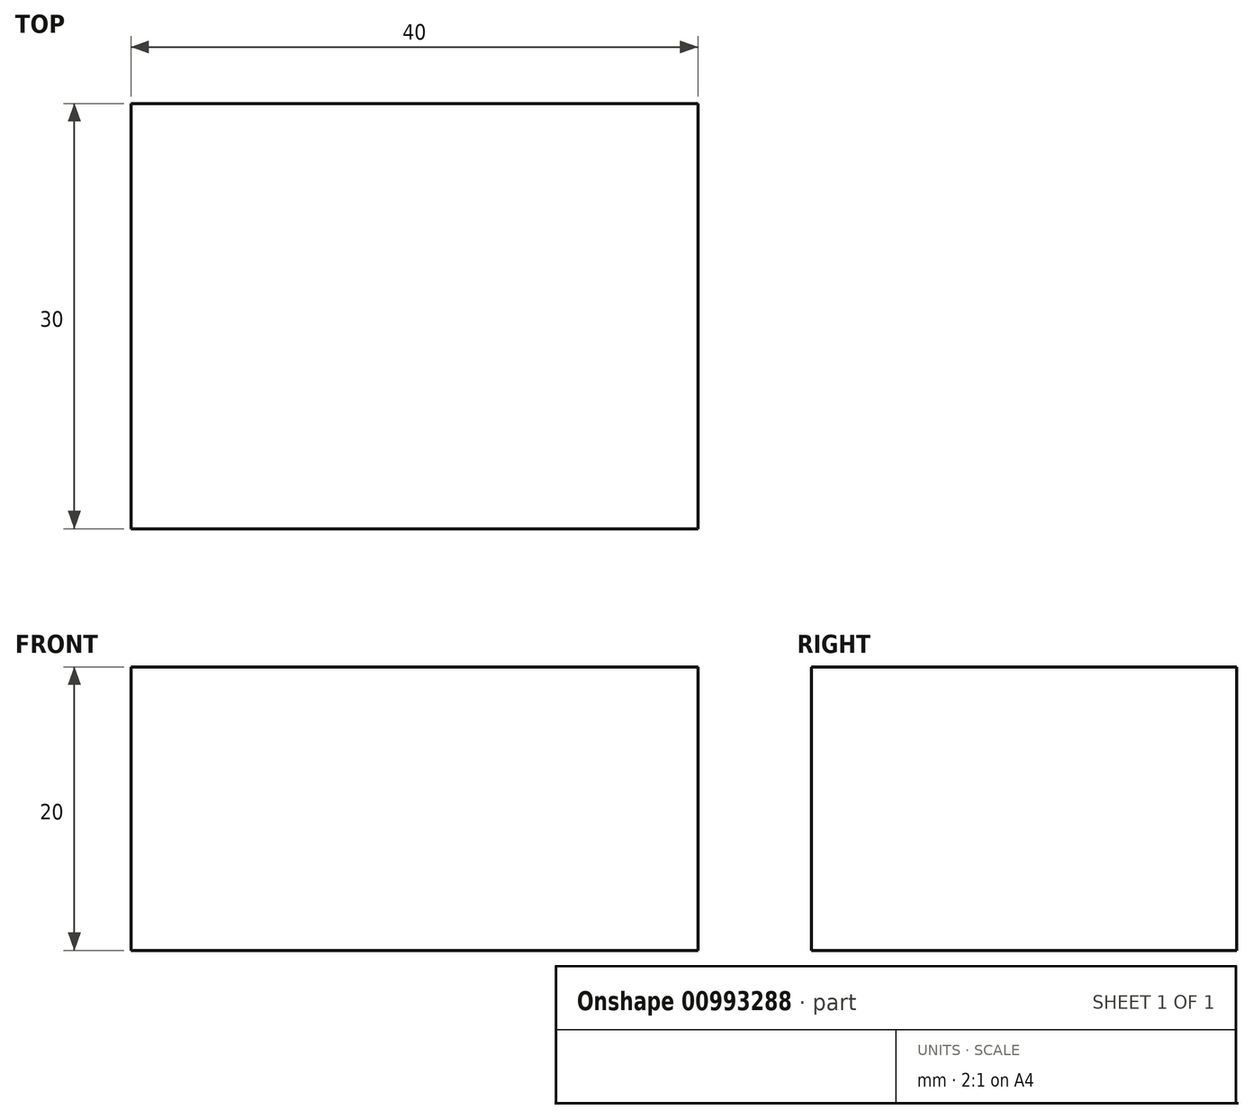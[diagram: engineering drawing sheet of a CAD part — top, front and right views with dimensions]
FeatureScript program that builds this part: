
annotation { "Feature Type Name" : "Feature", "Feature Type Description" : "" }
export const myFeature = defineFeature(function(context is Context, id is Id, definition is map)
    precondition{}
    {
        {
            var Q0;
            Q0=qCreatedBy(makeId("Top.planeOp"),FACE);
            var sketch = newSketch(context, id + "F0", { "sketchPlane" : qUnion([Q0])});
            skLineSegment(sketch, "E0.bottom", {"start": v(-53.22, 7.03) * mm, "end": v(-13.22, 7.03) * mm});
            skLineSegment(sketch, "E0.top", {"start": v(-53.22, -22.97) * mm, "end": v(-13.22, -22.97) * mm});
            skLineSegment(sketch, "E0.left", {"start": v(-53.22, 7.03) * mm, "end": v(-53.22, -22.97) * mm});
            skLineSegment(sketch, "E0.right", {"start": v(-13.22, 7.03) * mm, "end": v(-13.22, -22.97) * mm});
            skSolve(sketch);
        }
        {
            var Q0;
            Q0 = qSketchRegion(id + "F0", true);
            extrude(context, id + "F1", {"entities" : qUnion([Q0]), "depth" : 20 * mm, "offsetDistance" : 25 * mm});
        }
    });
